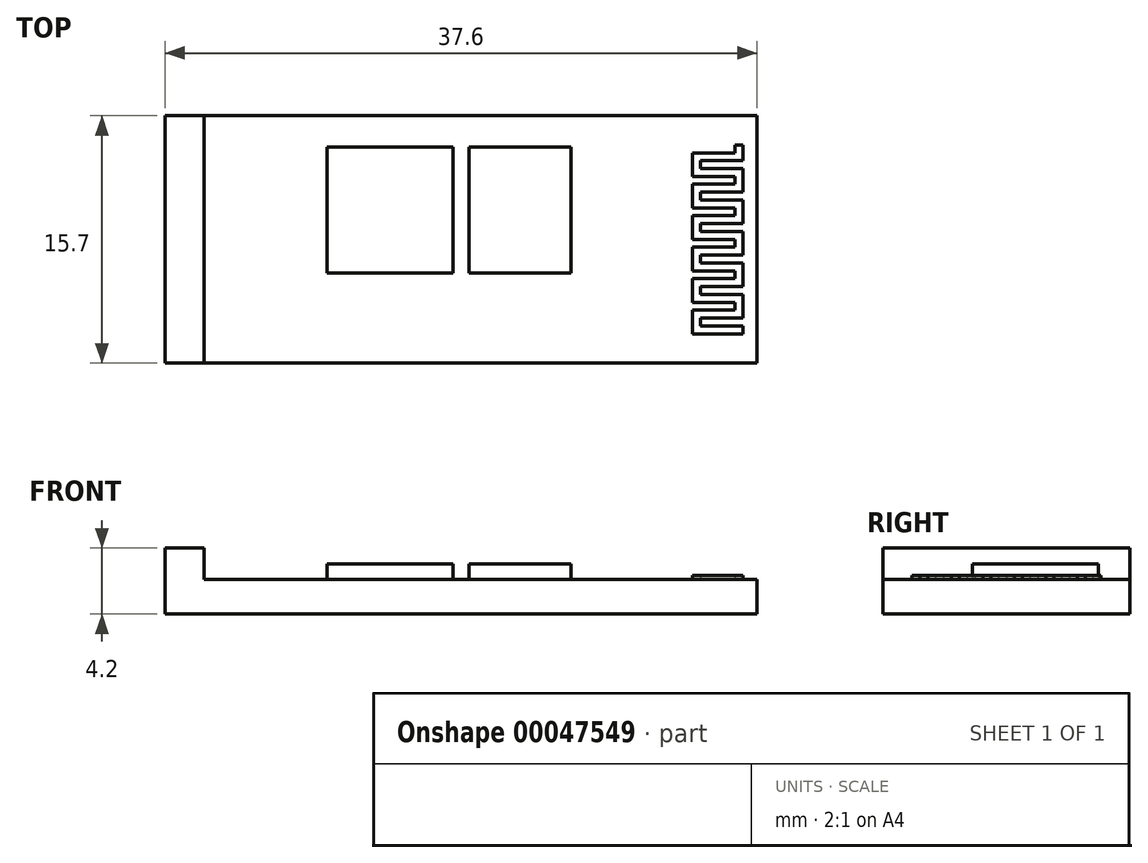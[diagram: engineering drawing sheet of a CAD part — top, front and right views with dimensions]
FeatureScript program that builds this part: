
annotation { "Feature Type Name" : "Feature", "Feature Type Description" : "" }
export const myFeature = defineFeature(function(context is Context, id is Id, definition is map)
    precondition{}
    {
        {
            var Q0;
            Q0=qCreatedBy(makeId("Top.planeOp"),FACE);
            var sketch = newSketch(context, id + "F0", { "sketchPlane" : qUnion([Q0])});
            skLineSegment(sketch, "E0.bottom", {"start": v(-18.8, 7.85) * mm, "end": v(18.8, 7.85) * mm});
            skLineSegment(sketch, "E0.top", {"start": v(-18.8, -7.85) * mm, "end": v(18.8, -7.85) * mm});
            skLineSegment(sketch, "E0.left", {"start": v(-18.8, 7.85) * mm, "end": v(-18.8, -7.85) * mm});
            skLineSegment(sketch, "E0.right", {"start": v(18.8, 7.85) * mm, "end": v(18.8, -7.85) * mm});
            skSolve(sketch);
        }
        {
            var Q0;
            Q0 = qSketchRegion(id + "F0", true);
            extrude(context, id + "F1", {"entities" : qUnion([Q0]), "depth" : 2.2 * mm});
        }
        {
            var Q0;
            Q0=makeQuery(id+"F1.opExtrude","CAP_FACE",FACE,{"disambiguationData":[OSD([sQuery(id+"F0.wireOp",EDGE,"E0.bottom"),sQuery(id+"F0.wireOp",EDGE,"E0.top"),sQuery(id+"F0.wireOp",EDGE,"E0.left"),sQuery(id+"F0.wireOp",EDGE,"E0.right")])],"isStart":false});
            var sketch = newSketch(context, id + "F2", { "sketchPlane" : qUnion([Q0])});
            skLineSegment(sketch, "E1.bottom", {"start": v(17.4, 6) * mm, "end": v(17.9, 6) * mm});
            skLineSegment(sketch, "E1.top", {"start": v(14.7, -6) * mm, "end": v(17.9, -6) * mm});
            skLineSegment(sketch, "E1.left", {"start": v(14.7, 5.5) * mm, "end": v(14.7, 4) * mm});
            skLineSegment(sketch, "E1.right", {"start": v(17.9, 6) * mm, "end": v(17.9, 5) * mm});
            skLineSegment(sketch, "E2", {"start": v(14.7, 5.5) * mm, "end": v(17.4, 5.5) * mm});
            skLineSegment(sketch, "E3", {"start": v(17.4, 6) * mm, "end": v(17.4, 5.5) * mm});
            skLineSegment(sketch, "E4.0", {"start": v(15.2, 5) * mm, "end": v(17.9, 5) * mm});
            skLineSegment(sketch, "E5", {"start": v(15.2, 5) * mm, "end": v(15.2, 4.5) * mm});
            skLineSegment(sketch, "E6.0", {"start": v(15.2, 4.5) * mm, "end": v(17.9, 4.5) * mm});
            skLineSegment(sketch, "E7.0", {"start": v(15.2, 4) * mm, "end": v(17.4, 4) * mm});
            skLineSegment(sketch, "E8.trimOffspring", {"start": v(15.2, 3) * mm, "end": v(15.2, 2.5) * mm});
            skLineSegment(sketch, "E9.trimOffspring", {"start": v(17.4, 4) * mm, "end": v(17.4, 3.5) * mm});
            skLineSegment(sketch, "E10.trimOffspring", {"start": v(17.9, 4.5) * mm, "end": v(17.9, 3) * mm});
            skLineSegment(sketch, "E11", {"start": v(14.7, 3.5) * mm, "end": v(17.4, 3.5) * mm});
            skLineSegment(sketch, "E12.0", {"start": v(14.7, 2) * mm, "end": v(17.4, 2) * mm});
            skLineSegment(sketch, "E13.0", {"start": v(14.7, 1.5) * mm, "end": v(17.4, 1.5) * mm});
            skLineSegment(sketch, "E14", {"start": v(15.2, 4) * mm, "end": v(14.7, 4) * mm});
            skLineSegment(sketch, "E15.trimOffspring", {"start": v(14.7, 3.5) * mm, "end": v(14.7, 2) * mm});
            skLineSegment(sketch, "E16.trimOffspring", {"start": v(15.2, 3) * mm, "end": v(17.9, 3) * mm});
            skLineSegment(sketch, "E17.trimOffspring", {"start": v(15.2, 2.5) * mm, "end": v(17.9, 2.5) * mm});
            skLineSegment(sketch, "E18.trimOffspring", {"start": v(17.4, 2) * mm, "end": v(17.4, 1.5) * mm});
            skLineSegment(sketch, "E19.trimOffspring", {"start": v(17.9, 2.5) * mm, "end": v(17.9, 1) * mm});
            skLineSegment(sketch, "E20.0", {"start": v(14.7, 0) * mm, "end": v(17.4, 0) * mm});
            skLineSegment(sketch, "E21.0", {"start": v(14.7, -0.5) * mm, "end": v(17.4, -0.5) * mm});
            skLineSegment(sketch, "E22.trimOffspring", {"start": v(17.4, 0) * mm, "end": v(17.4, -0.5) * mm});
            skLineSegment(sketch, "E23.trimOffspring", {"start": v(17.9, 0.5) * mm, "end": v(17.9, -1) * mm});
            skLineSegment(sketch, "E24.trimOffspring", {"start": v(15.2, 1) * mm, "end": v(15.2, 0.5) * mm});
            skLineSegment(sketch, "E25.trimOffspring", {"start": v(15.2, 1) * mm, "end": v(17.9, 1) * mm});
            skLineSegment(sketch, "E26.trimOffspring", {"start": v(14.7, 1.5) * mm, "end": v(14.7, 0) * mm});
            skLineSegment(sketch, "E27.trimOffspring", {"start": v(15.2, 0.5) * mm, "end": v(17.9, 0.5) * mm});
            skLineSegment(sketch, "E28.trimOffspring", {"start": v(15.2, -1) * mm, "end": v(15.2, -1.5) * mm});
            skLineSegment(sketch, "E29.trimOffspring", {"start": v(17.4, -2) * mm, "end": v(17.4, -2.5) * mm});
            skLineSegment(sketch, "E30.trimOffspring", {"start": v(14.7, -0.5) * mm, "end": v(14.7, -2) * mm});
            skLineSegment(sketch, "E31.0", {"start": v(14.7, -2) * mm, "end": v(17.4, -2) * mm});
            skLineSegment(sketch, "E32.0", {"start": v(14.7, -2.5) * mm, "end": v(17.4, -2.5) * mm});
            skLineSegment(sketch, "E33.0", {"start": v(14.7, -4) * mm, "end": v(17.4, -4) * mm});
            skLineSegment(sketch, "E34.trimOffspring", {"start": v(15.2, -1) * mm, "end": v(17.9, -1) * mm});
            skLineSegment(sketch, "E35.trimOffspring", {"start": v(15.2, -1.5) * mm, "end": v(17.9, -1.5) * mm});
            skLineSegment(sketch, "E36.trimOffspring", {"start": v(17.9, -1.5) * mm, "end": v(17.9, -3) * mm});
            skLineSegment(sketch, "E37.trimOffspring", {"start": v(15.2, -3) * mm, "end": v(15.2, -3.5) * mm});
            skLineSegment(sketch, "E38.trimOffspring", {"start": v(15.2, -3) * mm, "end": v(17.9, -3) * mm});
            skLineSegment(sketch, "E39.trimOffspring", {"start": v(14.7, -2.5) * mm, "end": v(14.7, -4) * mm});
            skLineSegment(sketch, "E40.trimOffspring", {"start": v(15.2, -3.5) * mm, "end": v(17.9, -3.5) * mm});
            skLineSegment(sketch, "E41.trimOffspring", {"start": v(17.4, -4) * mm, "end": v(17.4, -4.5) * mm});
            skLineSegment(sketch, "E42.trimOffspring", {"start": v(17.9, -3.5) * mm, "end": v(17.9, -5) * mm});
            skLineSegment(sketch, "E43.0", {"start": v(14.7, -4.5) * mm, "end": v(17.4, -4.5) * mm});
            skLineSegment(sketch, "E44.trimOffspring", {"start": v(15.2, -5) * mm, "end": v(15.2, -5.5) * mm});
            skLineSegment(sketch, "E45.trimOffspring", {"start": v(14.7, -4.5) * mm, "end": v(14.7, -6) * mm});
            skLineSegment(sketch, "E46.trimOffspring", {"start": v(15.2, -5) * mm, "end": v(17.9, -5) * mm});
            skLineSegment(sketch, "E47.trimOffspring", {"start": v(15.2, -5.5) * mm, "end": v(17.9, -5.5) * mm});
            skLineSegment(sketch, "E48.trimOffspring", {"start": v(17.9, -5.5) * mm, "end": v(17.9, -6) * mm});
            skSolve(sketch);
        }
        {
            var Q0;
            Q0 = qSketchRegion(id + "F2", true);
            extrude(context, id + "F3", {"entities" : qUnion([Q0]), "operationType" : NewBodyOperationType.ADD, "depth" : .25 * mm});
        }
        {
            var Q0;
            Q0=makeQuery(id+"F1.opExtrude","CAP_FACE",FACE,{"disambiguationData":[OSD([sQuery(id+"F0.wireOp",EDGE,"E0.bottom"),sQuery(id+"F0.wireOp",EDGE,"E0.top"),sQuery(id+"F0.wireOp",EDGE,"E0.left"),sQuery(id+"F0.wireOp",EDGE,"E0.right")])],"isStart":false});
            var sketch = newSketch(context, id + "F4", { "sketchPlane" : qUnion([Q0])});
            skLineSegment(sketch, "E49.bottom", {"start": v(-18.8, 7.85) * mm, "end": v(-16.3, 7.85) * mm});
            skLineSegment(sketch, "E49.top", {"start": v(-18.8, -7.85) * mm, "end": v(-16.3, -7.85) * mm});
            skLineSegment(sketch, "E49.left", {"start": v(-18.8, 7.85) * mm, "end": v(-18.8, -7.85) * mm});
            skLineSegment(sketch, "E49.right", {"start": v(-16.3, 7.85) * mm, "end": v(-16.3, -7.85) * mm});
            skSolve(sketch);
        }
        {
            var Q0;
            Q0 = qSketchRegion(id + "F4", true);
            extrude(context, id + "F5", {"entities" : qUnion([Q0]), "operationType" : NewBodyOperationType.ADD, "depth" : 2 * mm});
        }
        {
            var Q0;
            Q0=makeQuery(id+"F1.opExtrude","CAP_FACE",FACE,{"disambiguationData":[OSD([sQuery(id+"F0.wireOp",EDGE,"E0.bottom"),sQuery(id+"F0.wireOp",EDGE,"E0.top"),sQuery(id+"F0.wireOp",EDGE,"E0.left"),sQuery(id+"F0.wireOp",EDGE,"E0.right")])],"isStart":false});
            var sketch = newSketch(context, id + "F6", { "sketchPlane" : qUnion([Q0])});
            skLineSegment(sketch, "E50.bottom", {"start": v(-8.5, 5.85) * mm, "end": v(-0.5, 5.85) * mm});
            skLineSegment(sketch, "E50.top", {"start": v(-8.5, -2.15) * mm, "end": v(-0.5, -2.15) * mm});
            skLineSegment(sketch, "E50.left", {"start": v(-8.5, 5.85) * mm, "end": v(-8.5, -2.15) * mm});
            skLineSegment(sketch, "E50.right", {"start": v(-0.5, 5.85) * mm, "end": v(-0.5, -2.15) * mm});
            skLineSegment(sketch, "E51.bottom", {"start": v(0.5, 5.85) * mm, "end": v(7, 5.85) * mm});
            skLineSegment(sketch, "E51.top", {"start": v(0.5, -2.15) * mm, "end": v(7, -2.15) * mm});
            skLineSegment(sketch, "E51.left", {"start": v(0.5, 5.85) * mm, "end": v(0.5, -2.15) * mm});
            skLineSegment(sketch, "E51.right", {"start": v(7, 5.85) * mm, "end": v(7, -2.15) * mm});
            skSolve(sketch);
        }
        {
            var Q0;
            Q0 = qSketchRegion(id + "F6", true);
            extrude(context, id + "F7", {"entities" : qUnion([Q0]), "operationType" : NewBodyOperationType.ADD, "depth" : 1 * mm});
        }
    });
